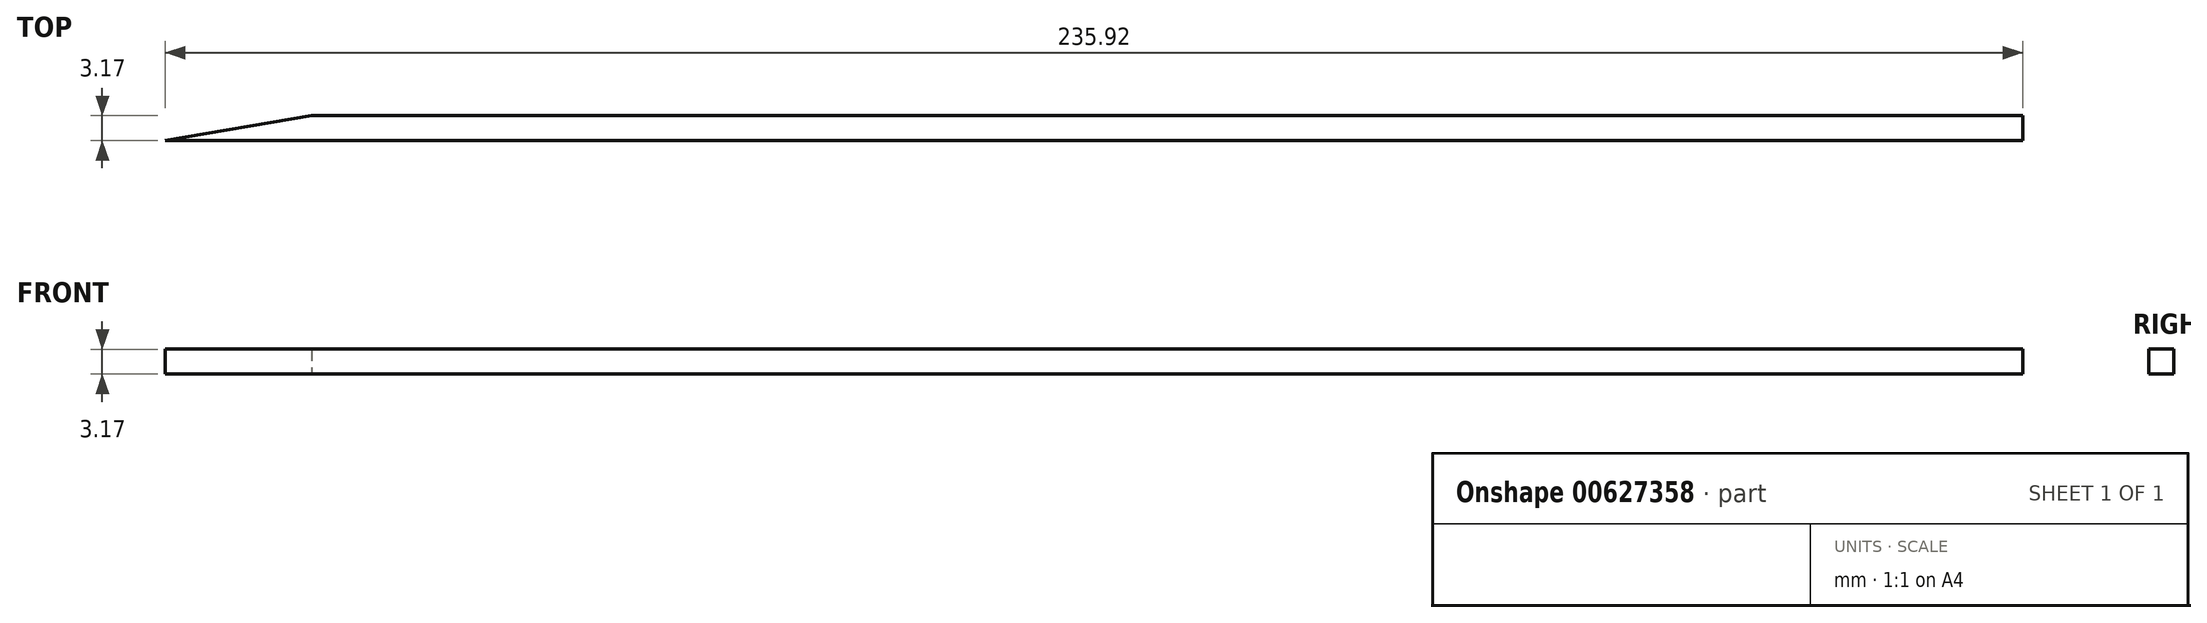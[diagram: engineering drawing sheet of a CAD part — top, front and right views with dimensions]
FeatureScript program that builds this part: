
annotation { "Feature Type Name" : "Feature", "Feature Type Description" : "" }
export const myFeature = defineFeature(function(context is Context, id is Id, definition is map)
    precondition{}
    {
        {
            var Q0;
            Q0=qCreatedBy(makeId("Top.planeOp"),FACE);
            var sketch = newSketch(context, id + "F0", { "sketchPlane" : qUnion([Q0])});
            skLineSegment(sketch, "E0", {"start": v(-100.24, 3.17) * mm, "end": v(117.11, 3.17) * mm});
            skLineSegment(sketch, "E1", {"start": v(117.11, 3.17) * mm, "end": v(117.11, 0) * mm});
            skLineSegment(sketch, "E2", {"start": v(117.11, 0) * mm, "end": v(-118.8, 0) * mm});
            skLineSegment(sketch, "E3", {"start": v(-118.8, 0) * mm, "end": v(-100.24, 3.17) * mm});
            skSolve(sketch);
        }
        {
            var Q0;
            Q0=makeQuery(id+"F0.imprint","IMPRINT",FACE,{"disambiguationData":[TD([[makeQuery(id+"F0.imprint","IMPRINT",EDGE,{"derivedFrom":sQuery(id+"F0.wireOp",EDGE,"E0")}),-1.0]])]});
            extrude(context, id + "F1", {"entities" : qUnion([Q0]), "depth" : 3.17 * mm, "offsetDistance" : 25.4 * mm});
        }
    });
